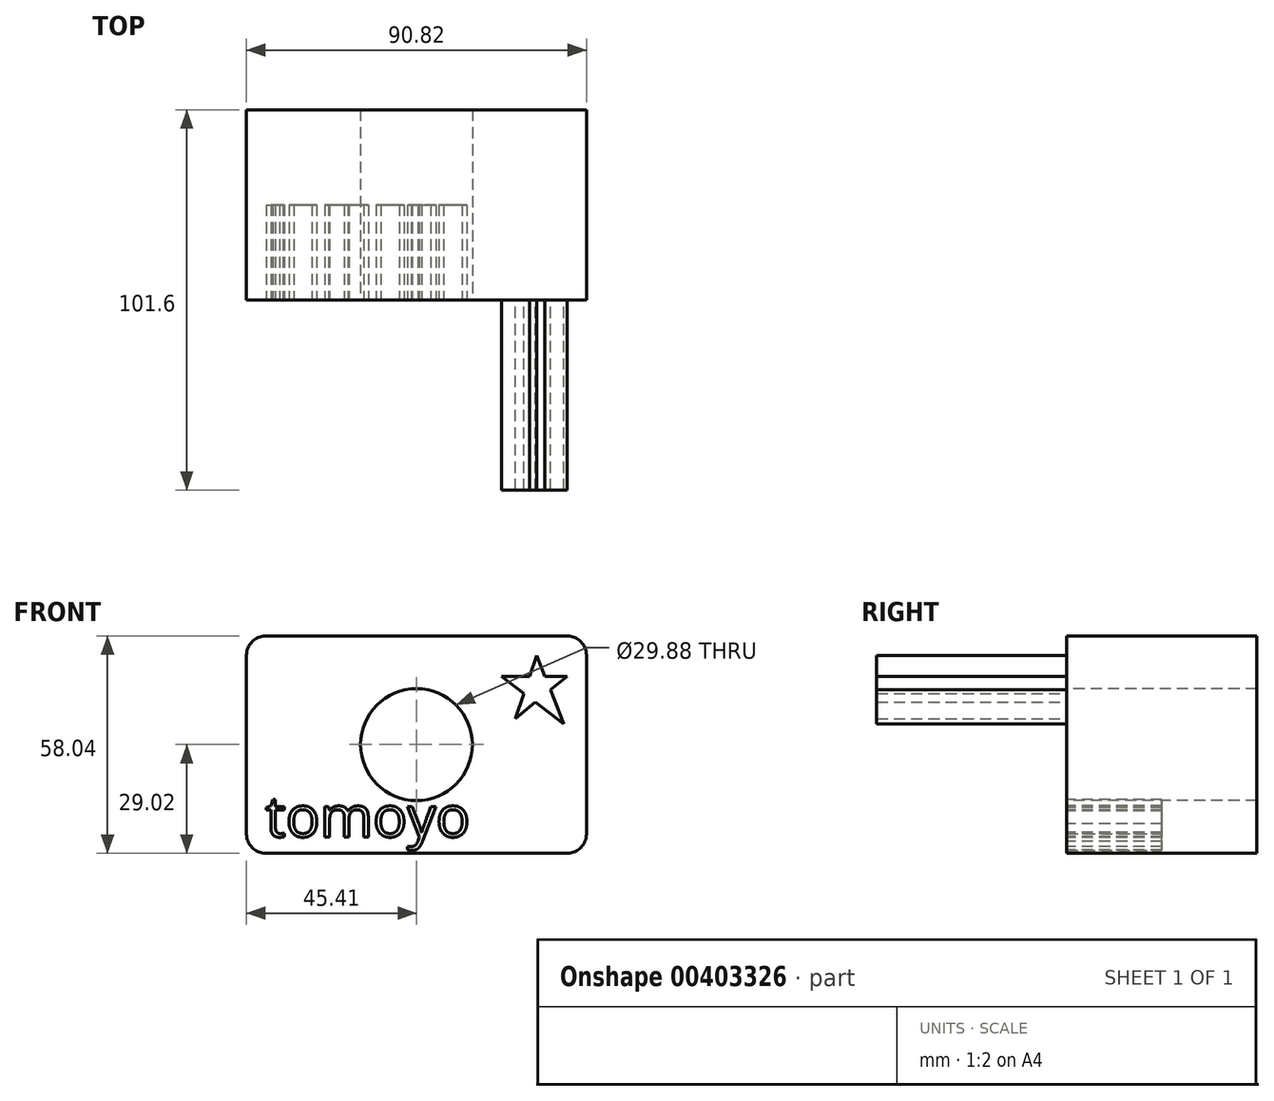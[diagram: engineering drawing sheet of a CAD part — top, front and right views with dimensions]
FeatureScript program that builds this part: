
annotation { "Feature Type Name" : "Feature", "Feature Type Description" : "" }
export const myFeature = defineFeature(function(context is Context, id is Id, definition is map)
    precondition{}
    {
        {
            var Q0;
            Q0=qCreatedBy(makeId("Front.planeOp"),FACE);
            var sketch = newSketch(context, id + "F0", { "sketchPlane" : qUnion([Q0])});
            skLineSegment(sketch, "E0.bottom", {"start": v(45.4, -29.02) * mm, "end": v(-45.4, -29.02) * mm});
            skLineSegment(sketch, "E0.top", {"start": v(45.4, 29.02) * mm, "end": v(-45.4, 29.02) * mm});
            skLineSegment(sketch, "E0.left", {"start": v(45.4, -29.02) * mm, "end": v(45.4, 29.02) * mm});
            skLineSegment(sketch, "E0.right", {"start": v(-45.4, -29.02) * mm, "end": v(-45.4, 29.02) * mm});
            skPoint(sketch, "E0.middle", {"position": v(0, 0) * mm});
            skSolve(sketch);
        }
        {
            var Q0;
            Q0 = qSketchRegion(id + "F0", true);
            extrude(context, id + "F1", {"entities" : qUnion([Q0]), "depth" : 50.8 * mm});
        }
        {
            var Q0;
            Q0=makeQuery(id+"F1.opExtrude","CAP_FACE",FACE,{"disambiguationData":[OSD([sQuery(id+"F0.wireOp",EDGE,"E0.bottom"),sQuery(id+"F0.wireOp",EDGE,"E0.top"),sQuery(id+"F0.wireOp",EDGE,"E0.left"),sQuery(id+"F0.wireOp",EDGE,"E0.right")])],"isStart":false});
            var sketch = newSketch(context, id + "F2", { "sketchPlane" : qUnion([Q0])});
            skSolve(sketch);
        }
        {
            var Q0;
            Q0=makeQuery(id+"F1.opExtrude","CAP_FACE",FACE,{"disambiguationData":[OSD([sQuery(id+"F0.wireOp",EDGE,"E0.bottom"),sQuery(id+"F0.wireOp",EDGE,"E0.top"),sQuery(id+"F0.wireOp",EDGE,"E0.left"),sQuery(id+"F0.wireOp",EDGE,"E0.right")])],"isStart":false});
            var sketch = newSketch(context, id + "F3", { "sketchPlane" : qUnion([Q0])});
            skCircle(sketch, "E1", {"center": v(0, 0) * mm, "radius": 14.94 * mm});
            skSolve(sketch);
        }
        {
            var Q0;
            Q0 = qSketchRegion(id + "F3", true);
            extrude(context, id + "F4", {"entities" : qUnion([Q0]), "operationType" : NewBodyOperationType.REMOVE, "oppositeDirection" : true, "depth" : 127 * mm});
        }
        {
            var Q0;
            Q0=makeQuery(id+"F1.opExtrude","SWEPT_EDGE",EDGE,{"disambiguationData":[OSD([sQuery(id+"F0.wireOp",EDGE,"E0.top"),sQuery(id+"F0.wireOp",EDGE,"E0.left")])]});
            fillet(context, id + "F5", {"entities" : qUnion([Q0]), "radius" : 5.08 * mm, "tangentPropagation" : true, "allowEdgeOverflow" : false});
        }
        {
            var Q0;
            Q0=makeQuery(id+"F1.opExtrude","SWEPT_EDGE",EDGE,{"disambiguationData":[OSD([sQuery(id+"F0.wireOp",EDGE,"E0.bottom"),sQuery(id+"F0.wireOp",EDGE,"E0.left")])]});
            fillet(context, id + "F6", {"entities" : qUnion([Q0]), "radius" : 5.08 * mm, "tangentPropagation" : true, "allowEdgeOverflow" : false});
        }
        {
            var Q0;
            Q0=makeQuery(id+"F1.opExtrude","SWEPT_EDGE",EDGE,{"disambiguationData":[OSD([sQuery(id+"F0.wireOp",EDGE,"E0.top"),sQuery(id+"F0.wireOp",EDGE,"E0.right")])]});
            fillet(context, id + "F7", {"entities" : qUnion([Q0]), "radius" : 5.08 * mm, "tangentPropagation" : true, "allowEdgeOverflow" : false});
        }
        {
            var Q0;
            Q0=makeQuery(id+"F1.opExtrude","SWEPT_EDGE",EDGE,{"disambiguationData":[OSD([sQuery(id+"F0.wireOp",EDGE,"E0.bottom"),sQuery(id+"F0.wireOp",EDGE,"E0.right")])]});
            fillet(context, id + "F8", {"entities" : qUnion([Q0]), "radius" : 5.08 * mm, "tangentPropagation" : true, "allowEdgeOverflow" : false});
        }
        {
            var Q0;
            Q0=makeQuery(id+"F2.imprint","IMPRINT",FACE,{"disambiguationData":[TD([[makeQuery(id+"F2.imprint","IMPRINT",EDGE,{"derivedFrom":makeQuery(id+"F1.opExtrude","CAP_EDGE",EDGE,{"disambiguationData":[OSD([sQuery(id+"F0.wireOp",EDGE,"E0.bottom")])],"isStart":false})}),-1.0]])]});
            var sketch = newSketch(context, id + "F9", { "sketchPlane" : qUnion([Q0])});
            skLineSegment(sketch, "E2", {"start": v(22.68, 18.28) * mm, "end": v(40.24, 18.28) * mm});
            skLineSegment(sketch, "E3", {"start": v(40.24, 18.28) * mm, "end": v(26.35, 6.95) * mm});
            skLineSegment(sketch, "E4", {"start": v(26.35, 6.95) * mm, "end": v(32.17, 23.8) * mm});
            skLineSegment(sketch, "E5", {"start": v(32.17, 23.8) * mm, "end": v(39.32, 5.52) * mm});
            skLineSegment(sketch, "E6", {"start": v(39.32, 5.52) * mm, "end": v(22.68, 18.28) * mm});
            skSolve(sketch);
        }
        {
            var Q0;
            Q0 = qSketchRegion(id + "F9", true);
            extrude(context, id + "F10", {"entities" : qUnion([Q0]), "operationType" : NewBodyOperationType.ADD, "depth" : 50.8 * mm});
        }
        {
            var Q0;
            Q0=makeQuery(id+"F2.imprint","IMPRINT",FACE,{"disambiguationData":[TD([[makeQuery(id+"F2.imprint","IMPRINT",EDGE,{"derivedFrom":makeQuery(id+"F1.opExtrude","CAP_EDGE",EDGE,{"disambiguationData":[OSD([sQuery(id+"F0.wireOp",EDGE,"E0.bottom")])],"isStart":false})}),-1.0]])]});
            var sketch = newSketch(context, id + "F11", { "sketchPlane" : qUnion([Q0])});
            skText(sketch, "E7", { "text": "tomoyo", "fontName": "OpenSans-Regular.ttf"});
            const initialGuessF11  = {"E7": [-0.0403, -0.02465, 1, 0, 0.01093]};
            skSetInitialGuess(sketch, initialGuessF11);
            skSolve(sketch);
        }
        {
            var Q0;
            Q0 = qSketchRegion(id + "F11", true);
            extrude(context, id + "F12", {"entities" : qUnion([Q0]), "operationType" : NewBodyOperationType.REMOVE, "oppositeDirection" : true, "depth" : 25.4 * mm});
        }
    });
